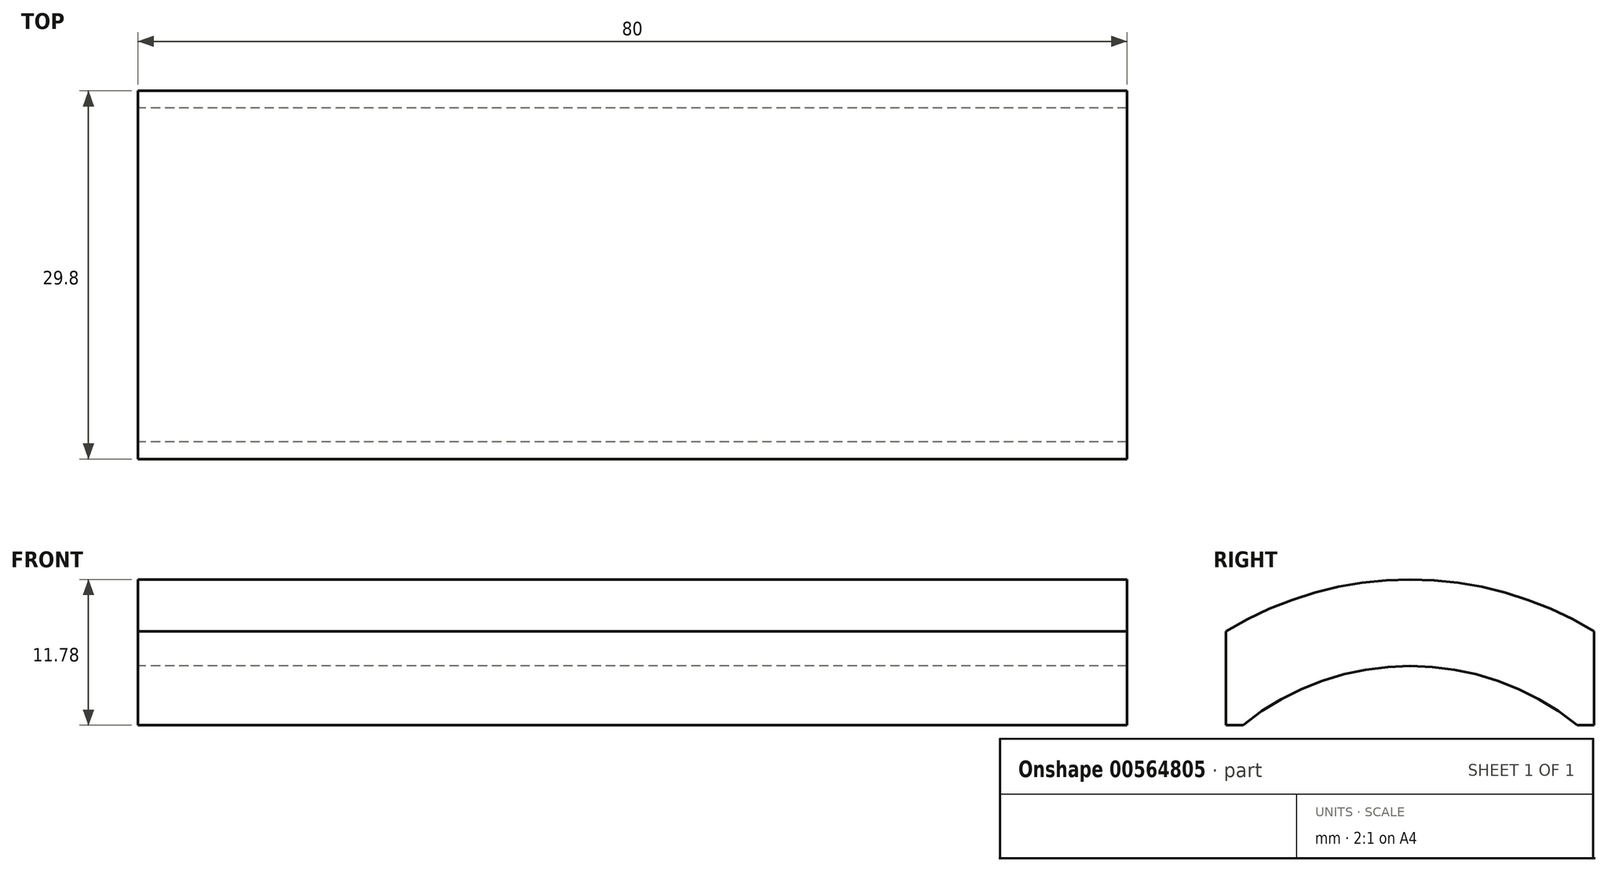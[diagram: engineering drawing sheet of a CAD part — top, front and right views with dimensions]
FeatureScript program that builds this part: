
annotation { "Feature Type Name" : "Feature", "Feature Type Description" : "" }
export const myFeature = defineFeature(function(context is Context, id is Id, definition is map)
    precondition{}
    {
        {
            var Q0;
            Q0=qCreatedBy(makeId("Right.planeOp"),FACE);
            var sketch = newSketch(context, id + "F0", { "sketchPlane" : qUnion([Q0])});
            skArc(sketch, "E0", {"start": v(14.9, 24.3) * mm, "mid": v(0, 28.5) * mm, "end": v(-14.9, 24.3) * mm});
            skArc(sketch, "E1.0", {"start": v(13.51, 16.72) * mm, "mid": v(0, 21.5) * mm, "end": v(-13.51, 16.72) * mm});
            skPoint(sketch, "E2", {"position": v(-14.9, 0) * mm});
            skPoint(sketch, "E3", {"position": v(14.9, 0) * mm});
            skLineSegment(sketch, "E4", {"start": v(-14.9, 16.72) * mm, "end": v(-14.9, 24.3) * mm});
            skLineSegment(sketch, "E5", {"start": v(14.9, 16.72) * mm, "end": v(14.9, 24.3) * mm});
            skPoint(sketch, "E6", {"position": v(0, 28.5) * mm});
            skPoint(sketch, "E7", {"position": v(0, 21.5) * mm});
            skPoint(sketch, "E8", {"position": v(-14.9, 16.72) * mm});
            skPoint(sketch, "E9", {"position": v(14.9, 16.72) * mm});
            skLineSegment(sketch, "E10", {"start": v(-14.9, 16.72) * mm, "end": v(-13.51, 16.72) * mm});
            skLineSegment(sketch, "E11", {"start": v(14.9, 16.72) * mm, "end": v(13.51, 16.72) * mm});
            skSolve(sketch);
        }
        {
            var Q0;
            Q0 = qSketchRegion(id + "F0", true);
            extrude(context, id + "F1", {"entities" : qUnion([Q0]), "depth" : 80 * mm, "offsetDistance" : 25 * mm});
        }
    });
